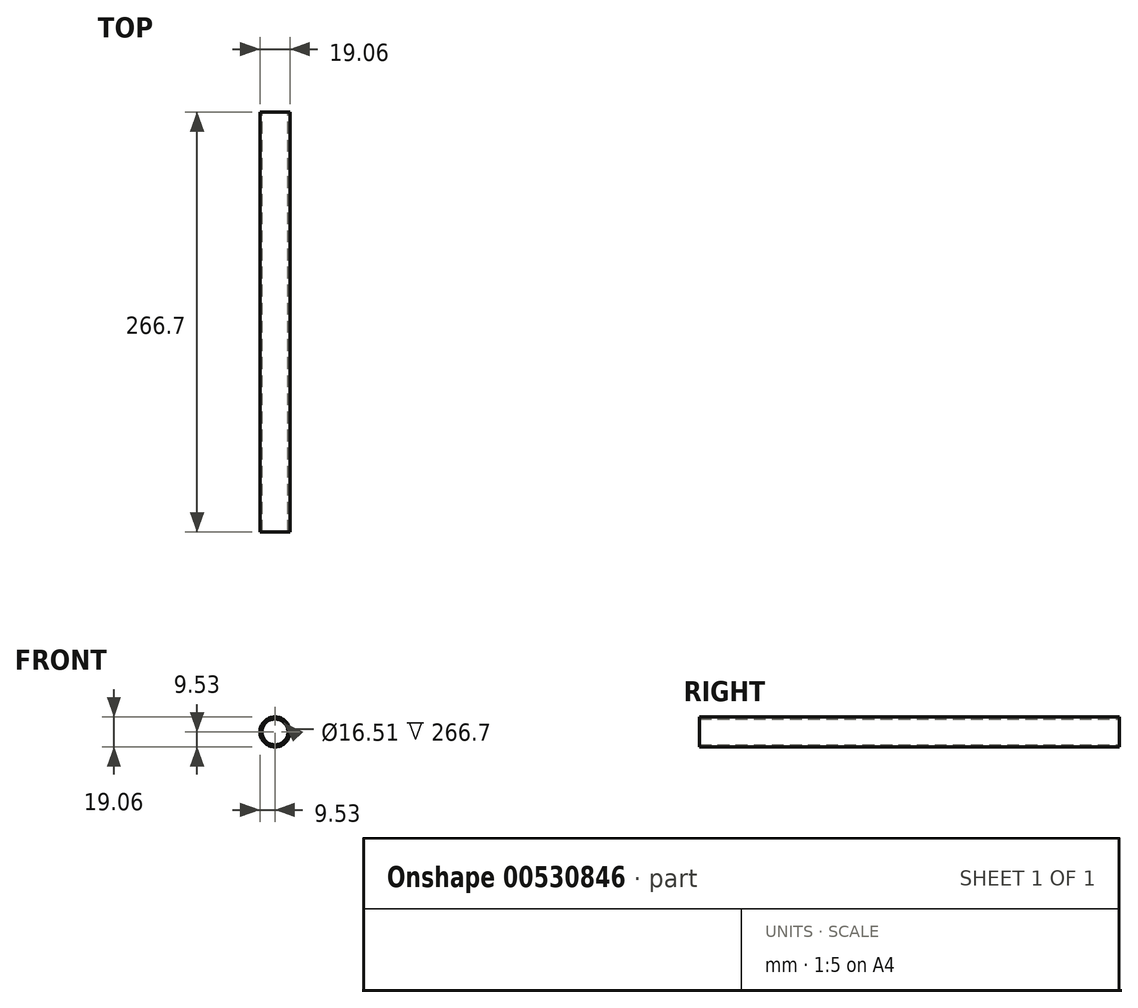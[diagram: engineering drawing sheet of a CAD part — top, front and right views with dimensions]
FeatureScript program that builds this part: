
annotation { "Feature Type Name" : "Feature", "Feature Type Description" : "" }
export const myFeature = defineFeature(function(context is Context, id is Id, definition is map)
    precondition{}
    {
        {
            var Q0;
            Q0=qCreatedBy(makeId("Front.planeOp"),FACE);
            var sketch = newSketch(context, id + "F0", { "sketchPlane" : qUnion([Q0])});
            skCircle(sketch, "E0", {"center": v(0, 0) * mm, "radius": 9.53 * mm});
            skSolve(sketch);
        }
        {
            var Q0;
            Q0 = qSketchRegion(id + "F0", true);
            extrude(context, id + "F1", {"entities" : qUnion([Q0]), "depth" : 266.7 * mm, "offsetDistance" : 25.4 * mm});
        }
        {
            var Q0;
            Q0=qCreatedBy(makeId("Front.planeOp"),FACE);
            var sketch = newSketch(context, id + "F2", { "sketchPlane" : qUnion([Q0])});
            skCircle(sketch, "E1", {"center": v(0, 0) * mm, "radius": 8.26 * mm});
            skSolve(sketch);
        }
        {
            var Q0;
            Q0 = qSketchRegion(id + "F2", true);
            extrude(context, id + "F3", {"entities" : qUnion([Q0]), "operationType" : NewBodyOperationType.REMOVE, "endBound" : BoundingType.THROUGH_ALL, "depth" : 266.7 * mm, "offsetDistance" : 25.4 * mm});
        }
    });
